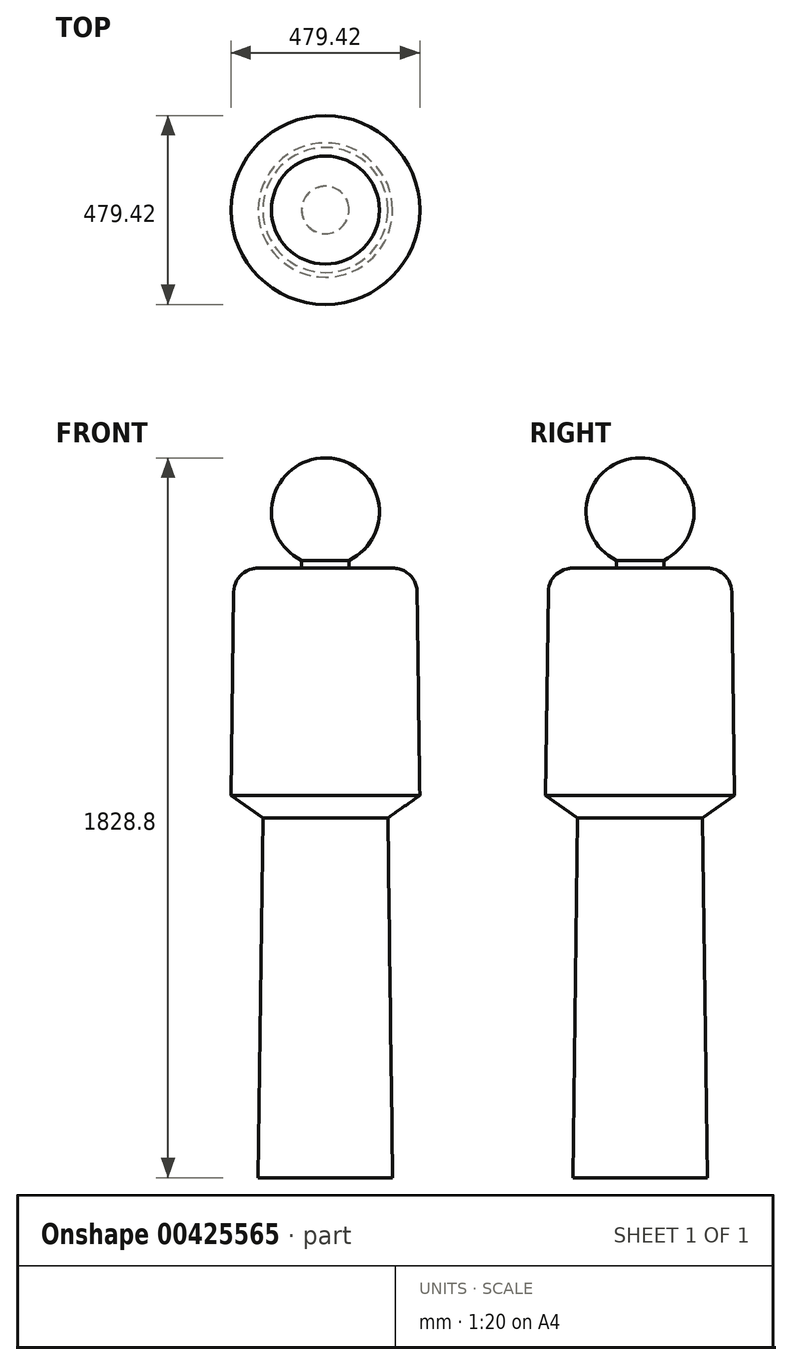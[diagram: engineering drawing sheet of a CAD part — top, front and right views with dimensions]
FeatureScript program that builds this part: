
annotation { "Feature Type Name" : "Feature", "Feature Type Description" : "" }
export const myFeature = defineFeature(function(context is Context, id is Id, definition is map)
    precondition{}
    {
        {
            var Q0;
            Q0=qCreatedBy(makeId("Front.planeOp"),FACE);
            var sketch = newSketch(context, id + "F0", { "sketchPlane" : qUnion([Q0])});
            skLineSegment(sketch, "E0.top", {"start": v(0, -914.4) * mm, "end": v(-170.66, -914.4) * mm});
            skLineSegment(sketch, "E0.right", {"start": v(-233, 574.03) * mm, "end": v(-239.7, 56.42) * mm});
            skPoint(sketch, "E0.middle", {"position": v(0, 0) * mm});
            skArc(sketch, "E1", {"start": v(0, 914.4) * mm, "mid": v(-133.64, 808.1) * mm, "end": v(-60.14, 653.97) * mm});
            skLineSegment(sketch, "E2", {"start": v(-60.14, 653.97) * mm, "end": v(-60.42, 632.76) * mm});
            skLineSegment(sketch, "E3", {"start": v(-60.42, 632.76) * mm, "end": v(-171.26, 634.2) * mm});
            skLineSegment(sketch, "E4", {"start": v(-239.7, 56.42) * mm, "end": v(-158.82, -0.08) * mm});
            skLineSegment(sketch, "E5", {"start": v(-158.82, -0.08) * mm, "end": v(-170.66, -914.4) * mm});
            skPoint(sketch, "E6.orphan", {"position": v(-252.27, -914.4) * mm});
            skPoint(sketch, "E7.orphan", {"position": v(-228.6, 914.4) * mm});
            skLineSegment(sketch, "E8", {"start": v(0, 914.4) * mm, "end": v(0, -914.4) * mm});
            skPoint(sketch, "E0.left.start.orphan", {"position": v(252.27, 914.4) * mm});
            skPoint(sketch, "E9.orphan", {"position": v(228.6, -914.4) * mm});
            skPoint(sketch, "E10.visualSharp", {"position": v(-232.22, 634.99) * mm});
            skArc(sketch, "E10.filletArc", {"start": v(-171.26, 634.2) * mm, "mid": v(-214.6, 616.9) * mm, "end": v(-233, 574.03) * mm});
            skSolve(sketch);
        }
        {
            var Q0;
            Q0 = qSketchRegion(id + "F0", true);
            var Q1;
            Q1=sQuery(id+"F0.wireOp",EDGE,"E8");
            revolve(context, id + "F1", {"entities" : qUnion([Q0]), "axis" : qUnion([Q1]), "revolveType" : RevolveType.FULL});
        }
    });
